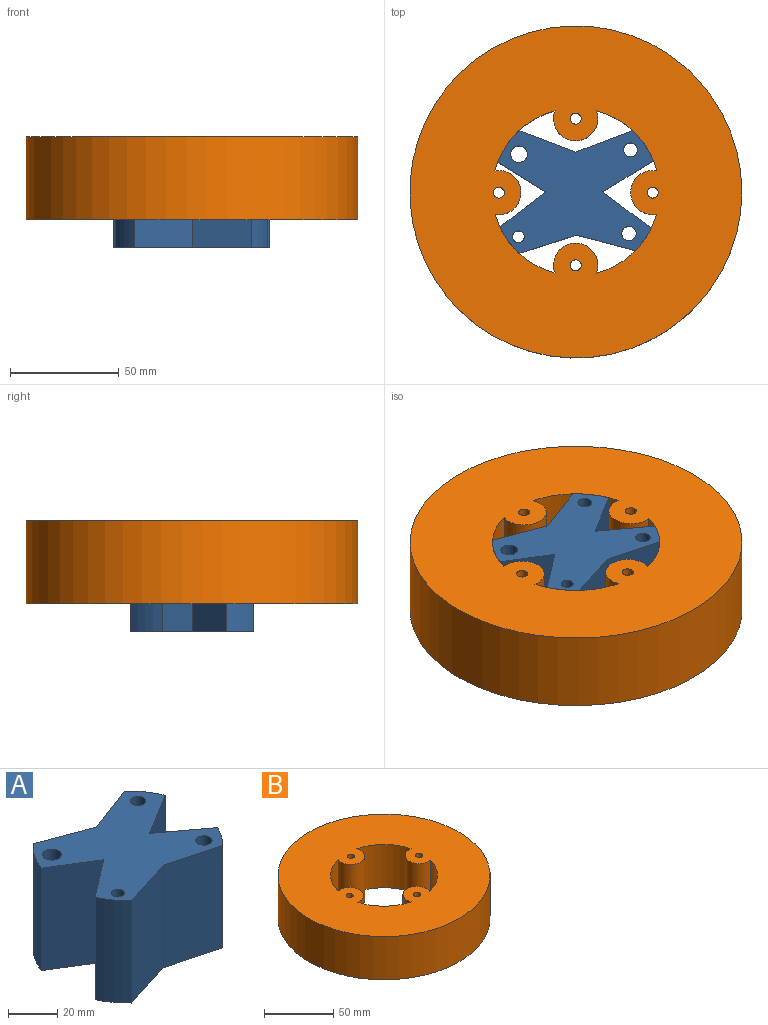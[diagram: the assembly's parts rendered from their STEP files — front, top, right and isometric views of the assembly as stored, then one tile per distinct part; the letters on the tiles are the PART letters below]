
ASSEMBLY  parts=2 mates=1
PART A: 18 faces, bbox 71.6x56.5x50.8 mm
  f0: plane 50.8x26.15mm, normal (0.35,0.94,0), area 1419.8mm2, adj f1,f14,f16,f17
  f1: cylinder r=38.48mm len=50.8mm, axis (0,0,-1), area 895.4mm2, adj f0,f2,f16,f17
  f2: plane 50.8x22.11mm, normal (-0.53,-0.85,0), area 1322.8mm2, adj f1,f3,f16,f17
  f3: plane 50.8x21.13mm, normal (-0.61,0.8,0), area 1349mm2, adj f2,f4,f16,f17
  f4: cylinder r=38.48mm len=50.8mm, axis (0,0,-1), area 767.2mm2, adj f3,f5,f16,f17
  f5: plane 50.8x26.63mm, normal (0.3,-0.95,0), area 1418mm2, adj f4,f6,f16,f17
  f6: plane 50.8x26.93mm, normal (-0.26,-0.97,0), area 1415.7mm2, adj f5,f7,f16,f17
  f7: cylinder r=38.48mm len=50.8mm, axis (0,0,-1), area 648.2mm2, adj f6,f8,f16,f17
  f8: plane 50.8x22.4mm, normal (0.6,0.8,0), area 1416.9mm2, adj f7,f9,f16,f17
  f9: plane 50.8x23.39mm, normal (0.52,-0.85,0), area 1394.4mm2, adj f8,f10,f16,f17
  f10: cylinder r=38.48mm len=50.8mm, axis (0,0,-1), area 861.9mm2, adj f9,f14,f16,f17
  f11: cylinder r=3.21mm len=50.8mm, axis (0,0,-1), area 1023.1mm2, adj f16,f17
  f12: cylinder r=3.31mm len=50.8mm, axis (0,0,-1), area 1055.9mm2, adj f16,f17
  f13: cylinder r=2.71mm len=50.8mm, axis (0,0,-1), area 865.7mm2, adj f16,f17
  f14: plane 50.8x26.15mm, normal (-0.35,0.94,0), area 1419.9mm2, adj f0,f10,f16,f17
  f15: cylinder r=3.83mm len=50.8mm, axis (0,0,-1), area 1221.7mm2, adj f16,f17
  f16: plane 71.64x56.46mm, normal (0,0,1), area 2475mm2, adj f0,f1,f2,f3,f4,f5,f6,f7
  f17: plane 71.64x56.46mm, normal (0,0,-1), area 2475mm2, adj f0,f1,f2,f3,f4,f5,f6,f7
PART B: 15 faces, bbox 152.7x152.7x38.1 mm
  f0: cylinder r=38.48mm len=38.1mm, axis (0,0,-1), area 1541mm2, adj f1,f7,f9,f10
  f1: cylinder r=10.16mm len=38.1mm, axis (0,0,-1), area 1494.3mm2, adj f0,f2,f9,f10
  f2: cylinder r=38.48mm len=38.1mm, axis (0,0,-1), area 1535.4mm2, adj f1,f3,f9,f10
  f3: cylinder r=10.16mm len=38.1mm, axis (0,0,-1), area 1350.4mm2, adj f2,f4,f9,f10
  f4: cylinder r=38.48mm len=38.1mm, axis (0,0,-1), area 1560.6mm2, adj f3,f5,f9,f10
  f5: cylinder r=10.16mm len=38.1mm, axis (0,0,-1), area 1494.3mm2, adj f4,f6,f9,f10
  f6: cylinder r=38.48mm len=38.1mm, axis (0,0,-1), area 1566.2mm2, adj f5,f7,f9,f10
  f7: cylinder r=10.16mm len=38.1mm, axis (0,0,-1), area 1350.4mm2, adj f0,f6,f9,f10
  f8: cylinder r=76.35mm len=152.7mm, axis (0,0,-1), area 18277mm2, adj f9,f10
  f9: plane 152.7x152.7mm, normal (0,0,1), area 14508.3mm2, adj f0,f1,f2,f3,f4,f5,f6,f7
  f10: plane 152.7x152.7mm, normal (0,0,-1), area 14508.3mm2, adj f0,f1,f2,f3,f4,f5,f6,f7
  f11: cylinder r=2.54mm len=38.1mm, axis (0,0,1), area 608mm2, adj f9,f10
  f12: cylinder r=2.54mm len=38.1mm, axis (0,0,1), area 608mm2, adj f9,f10
  f13: cylinder r=2.54mm len=38.1mm, axis (0,0,1), area 608mm2, adj f9,f10
  f14: cylinder r=2.54mm len=38.1mm, axis (0,0,1), area 608mm2, adj f9,f10
PLACE A t=(-18.4,-35.39,-1.81)mm
PLACE B t=(-18.97,-21.45,10.89)mm
MATE fastened B.f2 <-> A.f1  axis (0,0,1) through (-64.29,-21.46,48.99)mm
